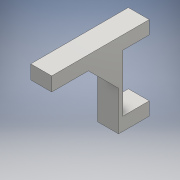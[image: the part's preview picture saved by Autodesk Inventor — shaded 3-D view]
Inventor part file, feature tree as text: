
AUTODESK INVENTOR PART (.ipt)
format: ipt  version: 2016 (Build 200138000, 138)  size: 123,904 bytes
history: native  units: mm
features: extrude x4, sketch x4
ambient origin geometry x8: Origin, YZ Plane, XZ Plane, XY Plane, X Axis, Y Axis, Z Axis, Center Point
bodies: Solid1 (feature_tree)
feature tree (8):
  extrude  "Extrusion1"  Depth=60.0mm
  extrude  "Extrusion2"  Depth=41.0mm
  extrude  "Extrusion3"  Depth=10.0mm
  extrude  "Extrusion5"  Depth=15.0mm TaperAngle=0.0deg
  sketch  "Sketch1"  dims[d0=15.0mm d1=60.0mm]
  sketch  "Sketch2"  dims[d2=3.0mm d3=0.0mm d4=41.0mm]
  sketch  "Sketch3"  dims[d5=19.0mm d6=0.0mm d7=10.0mm]
  sketch  "Sketch5"  dims[d8=48.0mm d9=15.0mm d10=0.0mm d15=45.0deg d16=15.0mm d17=0.0mm]
